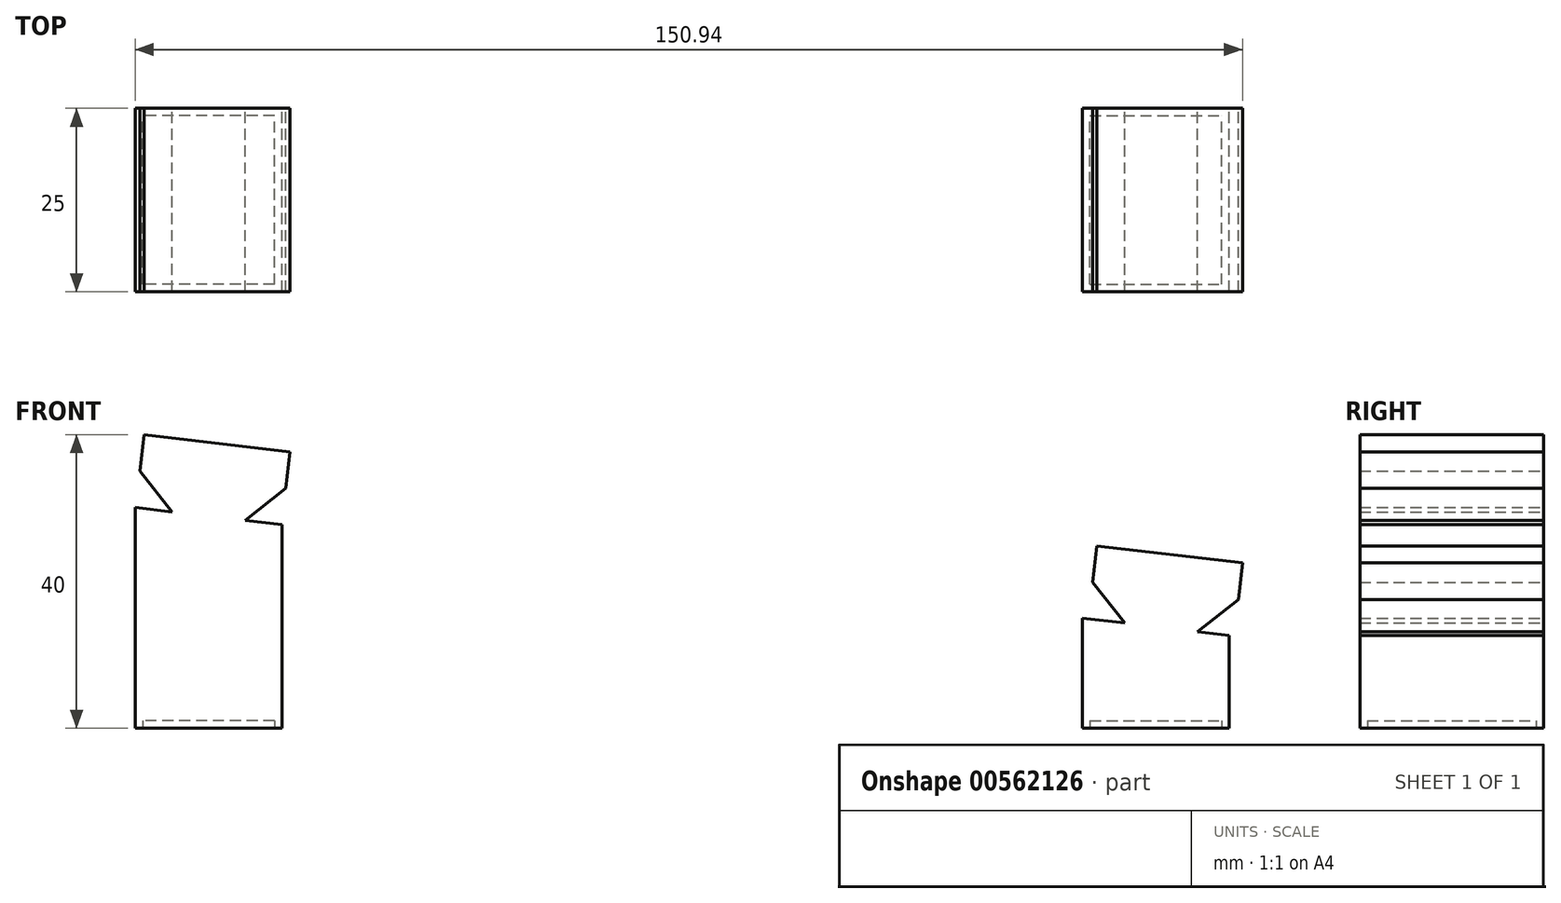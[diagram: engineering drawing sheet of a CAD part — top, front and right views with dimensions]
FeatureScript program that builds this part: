
annotation { "Feature Type Name" : "Feature", "Feature Type Description" : "" }
export const myFeature = defineFeature(function(context is Context, id is Id, definition is map)
    precondition{}
    {
        {
            var Q0;
            Q0=qCreatedBy(makeId("Front.planeOp"),FACE);
            var sketch = newSketch(context, id + "F0", { "sketchPlane" : qUnion([Q0])});
            skLineSegment(sketch, "E0.top", {"start": v(9.13, -10.76) * mm, "end": v(-10.87, -10.76) * mm});
            skLineSegment(sketch, "E1.bottom", {"start": v(9.64, 21.95) * mm, "end": v(-10.22, 24.27) * mm});
            skLineSegment(sketch, "E1.top", {"start": v(10.22, 26.92) * mm, "end": v(-9.64, 29.24) * mm});
            skLineSegment(sketch, "E1.left", {"start": v(9.64, 21.95) * mm, "end": v(10.22, 26.92) * mm});
            skLineSegment(sketch, "E1.right", {"start": v(-10.22, 24.27) * mm, "end": v(-9.64, 29.24) * mm});
            skPoint(sketch, "E1.middle", {"position": v(0, 25.6) * mm});
            skLineSegment(sketch, "E2", {"start": v(-10.22, 24.27) * mm, "end": v(-5.26, 23.69) * mm});
            skLineSegment(sketch, "E3", {"start": v(9.64, 21.95) * mm, "end": v(4.68, 22.53) * mm});
            skLineSegment(sketch, "E4", {"start": v(-5.26, 23.69) * mm, "end": v(-5.84, 18.72) * mm});
            skLineSegment(sketch, "E5", {"start": v(4.1, 17.56) * mm, "end": v(4.68, 22.53) * mm});
            skLineSegment(sketch, "E6", {"start": v(-10.87, -10.76) * mm, "end": v(9.13, -10.76) * mm});
            skLineSegment(sketch, "E7", {"start": v(9.13, -10.76) * mm, "end": v(9.13, 16.98) * mm});
            skLineSegment(sketch, "E8", {"start": v(9.13, 16.98) * mm, "end": v(-10.87, 19.31) * mm});
            skLineSegment(sketch, "E9", {"start": v(-10.87, 19.31) * mm, "end": v(-10.87, -10.76) * mm});
            skLineSegment(sketch, "E10", {"start": v(-10.87, 19.31) * mm, "end": v(-5.84, 18.72) * mm});
            skLineSegment(sketch, "E11", {"start": v(4.1, 17.56) * mm, "end": v(9.13, 16.98) * mm});
            skPoint(sketch, "E12.endSnap0", {"position": v(6.61, 17.27) * mm});
            skLineSegment(sketch, "E13", {"start": v(9.13, 16.98) * mm, "end": v(-10.87, 16.98) * mm});
            skLineSegment(sketch, "E14", {"start": v(-10.87, 19.31) * mm, "end": v(246.73, -10.76) * mm});
            skLineSegment(sketch, "E15", {"start": v(246.73, -10.76) * mm, "end": v(9.13, -10.76) * mm});
            skLineSegment(sketch, "E16", {"start": v(0, 25.6) * mm, "end": v(-0.87, 18.14) * mm});
            skLineSegment(sketch, "E17", {"start": v(-0.87, 18.14) * mm, "end": v(128.25, 3.07) * mm});
            skLineSegment(sketch, "E18", {"start": v(128.25, 3.07) * mm, "end": v(128.25, -10.76) * mm});
            skLineSegment(sketch, "E19", {"start": v(128.25, -10.76) * mm, "end": v(118.25, -10.76) * mm});
            skLineSegment(sketch, "E20", {"start": v(118.25, -10.76) * mm, "end": v(138.25, -10.76) * mm});
            skLineSegment(sketch, "E21", {"start": v(138.25, -10.76) * mm, "end": v(138.25, 1.9) * mm});
            skLineSegment(sketch, "E22", {"start": v(138.25, 1.9) * mm, "end": v(118.25, 4.24) * mm});
            skLineSegment(sketch, "E23", {"start": v(118.25, 4.24) * mm, "end": v(118.25, -10.76) * mm});
            skLineSegment(sketch, "E24", {"start": v(128.25, 3.07) * mm, "end": v(124.01, 3.56) * mm});
            skLineSegment(sketch, "E25", {"start": v(124.01, 3.56) * mm, "end": v(124.6, 8.53) * mm});
            skLineSegment(sketch, "E26", {"start": v(124.6, 8.53) * mm, "end": v(119.63, 9.1) * mm});
            skLineSegment(sketch, "E27", {"start": v(119.63, 9.1) * mm, "end": v(120.2, 14.08) * mm});
            skLineSegment(sketch, "E28", {"start": v(120.2, 14.08) * mm, "end": v(140.07, 11.76) * mm});
            skLineSegment(sketch, "E29", {"start": v(140.07, 11.76) * mm, "end": v(139.5, 6.8) * mm});
            skLineSegment(sketch, "E30", {"start": v(139.5, 6.8) * mm, "end": v(134.52, 7.37) * mm});
            skLineSegment(sketch, "E31", {"start": v(134.52, 7.37) * mm, "end": v(133.94, 2.4) * mm});
            skLineSegment(sketch, "E32", {"start": v(128.25, 3.07) * mm, "end": v(133.94, 2.4) * mm});
            skLineSegment(sketch, "E33", {"start": v(118.25, 4.24) * mm, "end": v(138.25, 1.9) * mm});
            skLineSegment(sketch, "E34", {"start": v(138.25, 1.9) * mm, "end": v(118.25, 1.9) * mm});
            skLineSegment(sketch, "E35", {"start": v(-10.22, 24.27) * mm, "end": v(-5.84, 18.72) * mm});
            skLineSegment(sketch, "E36", {"start": v(4.1, 17.56) * mm, "end": v(9.64, 21.95) * mm});
            skLineSegment(sketch, "E37", {"start": v(119.63, 9.1) * mm, "end": v(124.01, 3.56) * mm});
            skLineSegment(sketch, "E38", {"start": v(133.94, 2.4) * mm, "end": v(139.5, 6.8) * mm});
            skSolve(sketch);
        }
        {
            var Q0;
            {var subQ0=sQuery(id+"F0.wireOp",EDGE,"E0.top");Q0=makeQuery(id+"F0.imprint","IMPRINT",FACE,{"disambiguationData":[TD([[makeQuery(id+"F0.imprint","IMPRINT",EDGE,{"derivedFrom":subQ0}),-1.0]])]});}
            var Q1;
            {var subQ4=sQuery(id+"F0.wireOp",EDGE,"E13");Q1=makeQuery(id+"F0.imprint","IMPRINT",FACE,{"disambiguationData":[TD([[makeQuery(id+"F0.imprint","IMPRINT",EDGE,{"derivedFrom":subQ4}),-1.0]])]});}
            var Q2;
            {var subQ0=sQuery(id+"F0.wireOp",EDGE,"E4");Q2=makeQuery(id+"F0.imprint","IMPRINT",FACE,{"disambiguationData":[TD([[makeQuery(id+"F0.imprint","IMPRINT",EDGE,{"derivedFrom":subQ0}),1.0]])]});}
            var Q3;
            Q3=makeQuery(id+"F0.imprint","IMPRINT",FACE,{"disambiguationData":[TD([[makeQuery(id+"F0.imprint","IMPRINT",EDGE,{"derivedFrom":sQuery(id+"F0.wireOp",EDGE,"E1.top")}),1.0]])]});
            var Q4;
            {var subQ0=sQuery(id+"F0.wireOp",EDGE,"E5");Q4=makeQuery(id+"F0.imprint","IMPRINT",FACE,{"disambiguationData":[TD([[makeQuery(id+"F0.imprint","IMPRINT",EDGE,{"derivedFrom":subQ0}),1.0]])]});}
            var Q5;
            {var subQ0=sQuery(id+"F0.wireOp",EDGE,"E25");Q5=makeQuery(id+"F0.imprint","IMPRINT",FACE,{"disambiguationData":[TD([[makeQuery(id+"F0.imprint","IMPRINT",EDGE,{"derivedFrom":subQ0}),-1.0]])]});}
            var Q6;
            {var subQ0=sQuery(id+"F0.wireOp",EDGE,"E23");var subQ1=sQuery(id+"F0.wireOp",EDGE,"E15");var subQ2=makeQuery(id+"F0.imprint","INTERSECT",VERTEX,{"derivedFrom":[subQ1,subQ0]});Q6=makeQuery(id+"F0.imprint","IMPRINT",FACE,{"disambiguationData":[TD([[makeQuery(id+"F0.imprint","IMPRINT",EDGE,{"disambiguationData":[TD([[subQ2,1.0]])],"derivedFrom":subQ1}),-1.0]])]});}
            var Q7;
            {var subQ0=sQuery(id+"F0.wireOp",EDGE,"E21");Q7=makeQuery(id+"F0.imprint","IMPRINT",FACE,{"disambiguationData":[TD([[makeQuery(id+"F0.imprint","IMPRINT",EDGE,{"derivedFrom":subQ0}),1.0]])]});}
            var Q8;
            {var subQ0=sQuery(id+"F0.wireOp",EDGE,"E18");var subQ1=sQuery(id+"F0.wireOp",EDGE,"E14");var subQ2=makeQuery(id+"F0.imprint","INTERSECT",VERTEX,{"derivedFrom":[subQ1,subQ0]});Q8=makeQuery(id+"F0.imprint","IMPRINT",FACE,{"disambiguationData":[TD([[makeQuery(id+"F0.imprint","IMPRINT",EDGE,{"disambiguationData":[TD([[subQ2,-1.0]])],"derivedFrom":subQ0}),1.0]])]});}
            var Q9;
            {var subQ3=sQuery(id+"F0.wireOp",EDGE,"E14");var subQ5=sQuery(id+"F0.wireOp",EDGE,"E18");var subQ6=makeQuery(id+"F0.imprint","INTERSECT",VERTEX,{"derivedFrom":[subQ3,subQ5]});Q9=makeQuery(id+"F0.imprint","IMPRINT",FACE,{"disambiguationData":[TD([[makeQuery(id+"F0.imprint","IMPRINT",EDGE,{"disambiguationData":[TD([[subQ6,-1.0]])],"derivedFrom":subQ5}),-1.0]])]});}
            var Q10;
            {var subQ0=sQuery(id+"F0.wireOp",EDGE,"E5");Q10=makeQuery(id+"F0.imprint","IMPRINT",FACE,{"disambiguationData":[TD([[makeQuery(id+"F0.imprint","IMPRINT",EDGE,{"derivedFrom":subQ0}),-1.0]])]});}
            var Q11;
            {var subQ0=sQuery(id+"F0.wireOp",EDGE,"E4");Q11=makeQuery(id+"F0.imprint","IMPRINT",FACE,{"disambiguationData":[TD([[makeQuery(id+"F0.imprint","IMPRINT",EDGE,{"derivedFrom":subQ0}),-1.0]])]});}
            var Q12;
            Q12=makeQuery(id+"F0.imprint","IMPRINT",FACE,{"disambiguationData":[TD([[makeQuery(id+"F0.imprint","IMPRINT",EDGE,{"derivedFrom":sQuery(id+"F0.wireOp",EDGE,"E30")}),1.0]])]});
            var Q13;
            Q13=makeQuery(id+"F0.imprint","IMPRINT",FACE,{"disambiguationData":[TD([[makeQuery(id+"F0.imprint","IMPRINT",EDGE,{"derivedFrom":sQuery(id+"F0.wireOp",EDGE,"E25")}),1.0]])]});
            extrude(context, id + "F1", {"entities" : qUnion([Q0, Q1, Q2, Q3, Q4, Q5, Q6, Q7, Q8, Q9, Q10, Q11, Q12, Q13]), "endBound" : BoundingType.SYMMETRIC, "depth" : 25 * mm, "offsetDistance" : 25 * mm});
        }
        {
            var Q0;
            Q0=makeQuery(id+"F1.opExtrude","SWEPT_FACE",FACE,{"disambiguationData":[OSD([sQuery(id+"F0.wireOp",EDGE,"E15")])]});
            var sketch = newSketch(context, id + "F2", { "sketchPlane" : qUnion([Q0])});
            skLineSegment(sketch, "E39", {"start": v(118.25, 12.5) * mm, "end": v(138.25, 12.5) * mm});
            skLineSegment(sketch, "E40", {"start": v(138.25, 12.5) * mm, "end": v(138.25, -12.5) * mm});
            skLineSegment(sketch, "E41", {"start": v(138.25, -12.5) * mm, "end": v(118.25, -12.5) * mm});
            skLineSegment(sketch, "E42", {"start": v(118.25, -12.5) * mm, "end": v(118.25, 12.5) * mm});
            skLineSegment(sketch, "E43", {"start": v(128.25, 12.5) * mm, "end": v(128.25, -12.5) * mm});
            skLineSegment(sketch, "E44", {"start": v(128.25, -12.5) * mm, "end": v(128.25, 0) * mm});
            skLineSegment(sketch, "E45", {"start": v(128.25, 0) * mm, "end": v(118.25, 0) * mm});
            skLineSegment(sketch, "E46", {"start": v(118.25, 0) * mm, "end": v(138.25, 0) * mm});
            skLineSegment(sketch, "E47.bottom", {"start": v(119.25, 11.5) * mm, "end": v(137.25, 11.5) * mm});
            skLineSegment(sketch, "E47.top", {"start": v(119.25, -11.5) * mm, "end": v(137.25, -11.5) * mm});
            skLineSegment(sketch, "E47.left", {"start": v(119.25, 11.5) * mm, "end": v(119.25, -11.5) * mm});
            skLineSegment(sketch, "E47.right", {"start": v(137.25, 11.5) * mm, "end": v(137.25, -11.5) * mm});
            skPoint(sketch, "E47.middle", {"position": v(128.25, 0) * mm});
            skSolve(sketch);
        }
        {
            var Q0;
            Q0=makeQuery(id+"F1.opExtrude","SWEPT_FACE",FACE,{"disambiguationData":[OSD([sQuery(id+"F0.wireOp",EDGE,"E0.top")])]});
            var sketch = newSketch(context, id + "F3", { "sketchPlane" : qUnion([Q0])});
            skLineSegment(sketch, "E48", {"start": v(-10.87, 12.5) * mm, "end": v(9.13, 12.5) * mm});
            skLineSegment(sketch, "E49", {"start": v(9.13, 12.5) * mm, "end": v(9.13, -12.5) * mm});
            skLineSegment(sketch, "E50", {"start": v(9.13, -12.5) * mm, "end": v(-10.87, -12.5) * mm});
            skLineSegment(sketch, "E51", {"start": v(-10.87, -12.5) * mm, "end": v(-10.87, 12.5) * mm});
            skLineSegment(sketch, "E52", {"start": v(-0.87, 12.5) * mm, "end": v(-0.87, -12.5) * mm});
            skLineSegment(sketch, "E53", {"start": v(-10.87, 0) * mm, "end": v(9.13, 0) * mm});
            skLineSegment(sketch, "E54.bottom", {"start": v(8.13, 11.5) * mm, "end": v(-9.87, 11.5) * mm});
            skLineSegment(sketch, "E54.top", {"start": v(8.13, -11.5) * mm, "end": v(-9.87, -11.5) * mm});
            skLineSegment(sketch, "E54.left", {"start": v(8.13, 11.5) * mm, "end": v(8.13, -11.5) * mm});
            skLineSegment(sketch, "E54.right", {"start": v(-9.87, 11.5) * mm, "end": v(-9.87, -11.5) * mm});
            skPoint(sketch, "E54.middle", {"position": v(-0.87, 0) * mm});
            skSolve(sketch);
        }
        {
            var Q0;
            {var subQ0=sQuery(id+"F3.wireOp",EDGE,"E54.bottom");var subQ1=sQuery(id+"F3.wireOp",EDGE,"E52");var subQ2=makeQuery(id+"F3.imprint","INTERSECT",VERTEX,{"derivedFrom":[subQ1,subQ0]});Q0=makeQuery(id+"F3.imprint","IMPRINT",FACE,{"disambiguationData":[TD([[makeQuery(id+"F3.imprint","IMPRINT",EDGE,{"disambiguationData":[TD([[subQ2,-1.0]])],"derivedFrom":subQ1}),-1.0]])]});}
            var Q1;
            {var subQ0=sQuery(id+"F3.wireOp",EDGE,"E54.bottom");var subQ1=sQuery(id+"F3.wireOp",EDGE,"E52");var subQ2=makeQuery(id+"F3.imprint","INTERSECT",VERTEX,{"derivedFrom":[subQ1,subQ0]});Q1=makeQuery(id+"F3.imprint","IMPRINT",FACE,{"disambiguationData":[TD([[makeQuery(id+"F3.imprint","IMPRINT",EDGE,{"disambiguationData":[TD([[subQ2,-1.0]])],"derivedFrom":subQ1}),1.0]])]});}
            var Q2;
            {var subQ0=sQuery(id+"F3.wireOp",EDGE,"E53");var subQ1=sQuery(id+"F3.wireOp",EDGE,"E52");var subQ2=makeQuery(id+"F3.imprint","INTERSECT",VERTEX,{"derivedFrom":[subQ1,subQ0]});Q2=makeQuery(id+"F3.imprint","IMPRINT",FACE,{"disambiguationData":[TD([[makeQuery(id+"F3.imprint","IMPRINT",EDGE,{"disambiguationData":[TD([[subQ2,-1.0]])],"derivedFrom":subQ1}),1.0]])]});}
            var Q3;
            {var subQ0=sQuery(id+"F3.wireOp",EDGE,"E53");var subQ1=sQuery(id+"F3.wireOp",EDGE,"E52");var subQ2=makeQuery(id+"F3.imprint","INTERSECT",VERTEX,{"derivedFrom":[subQ1,subQ0]});Q3=makeQuery(id+"F3.imprint","IMPRINT",FACE,{"disambiguationData":[TD([[makeQuery(id+"F3.imprint","IMPRINT",EDGE,{"disambiguationData":[TD([[subQ2,-1.0]])],"derivedFrom":subQ1}),-1.0]])]});}
            extrude(context, id + "F4", {"entities" : qUnion([Q0, Q1, Q2, Q3]), "operationType" : NewBodyOperationType.REMOVE, "oppositeDirection" : true, "depth" : 1 * mm, "offsetDistance" : 25 * mm});
        }
        {
            var Q0;
            {var subQ3=sQuery(id+"F2.wireOp",EDGE,"E47.bottom");var subQ5=sQuery(id+"F2.wireOp",EDGE,"E47.right");var subQ7=makeQuery(id+"F2.imprint","INTERSECT",VERTEX,{"derivedFrom":[subQ3,subQ5]});Q0=makeQuery(id+"F2.imprint","IMPRINT",FACE,{"disambiguationData":[TD([[makeQuery(id+"F2.imprint","IMPRINT",EDGE,{"disambiguationData":[TD([[subQ7,1.0]])],"derivedFrom":subQ3}),-1.0]])]});}
            var Q1;
            {var subQ3=sQuery(id+"F2.wireOp",EDGE,"E47.top");var subQ5=sQuery(id+"F2.wireOp",EDGE,"E47.right");var subQ7=makeQuery(id+"F2.imprint","INTERSECT",VERTEX,{"derivedFrom":[subQ3,subQ5]});Q1=makeQuery(id+"F2.imprint","IMPRINT",FACE,{"disambiguationData":[TD([[makeQuery(id+"F2.imprint","IMPRINT",EDGE,{"disambiguationData":[TD([[subQ7,1.0]])],"derivedFrom":subQ3}),1.0]])]});}
            var Q2;
            {var subQ3=sQuery(id+"F2.wireOp",EDGE,"E47.top");var subQ5=sQuery(id+"F2.wireOp",EDGE,"E47.left");var subQ6=makeQuery(id+"F2.imprint","INTERSECT",VERTEX,{"derivedFrom":[subQ3,subQ5]});Q2=makeQuery(id+"F2.imprint","IMPRINT",FACE,{"disambiguationData":[TD([[makeQuery(id+"F2.imprint","IMPRINT",EDGE,{"disambiguationData":[TD([[subQ6,-1.0]])],"derivedFrom":subQ3}),1.0]])]});}
            var Q3;
            {var subQ3=sQuery(id+"F2.wireOp",EDGE,"E47.bottom");var subQ5=sQuery(id+"F2.wireOp",EDGE,"E47.left");var subQ7=makeQuery(id+"F2.imprint","INTERSECT",VERTEX,{"derivedFrom":[subQ3,subQ5]});Q3=makeQuery(id+"F2.imprint","IMPRINT",FACE,{"disambiguationData":[TD([[makeQuery(id+"F2.imprint","IMPRINT",EDGE,{"disambiguationData":[TD([[subQ7,-1.0]])],"derivedFrom":subQ3}),-1.0]])]});}
            extrude(context, id + "F5", {"entities" : qUnion([Q0, Q1, Q2, Q3]), "operationType" : NewBodyOperationType.REMOVE, "oppositeDirection" : true, "depth" : 1 * mm, "offsetDistance" : 25 * mm});
        }
    });
